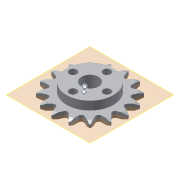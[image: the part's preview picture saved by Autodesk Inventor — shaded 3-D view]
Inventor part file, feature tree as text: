
AUTODESK INVENTOR PART (.ipt)
format: ipt  version: 2013 (Build 170138000, 138)  size: 427,520 bytes
history: native  units: in
note: dims shown in document units (in); Inventor stores cm internally (conversion verified against a paired STEP export)
features: other x17, plane x1
ambient origin geometry x8: Origin, YZ Plane, XZ Plane, XY Plane, X Axis, Y Axis, Z Axis, Center Point
bodies: Solid1 (feature_tree)
feature tree (18):
  other  "Tetrix sprocket 16T.ipt"
  other  "sprocket_25_16t_tetrix::Tetrix sprocket 16T.ipt"
  other  "TaggingFeature1"
  other  "FRONT"
  other  "TOP"
  other  "RIGHT"
  plane  "Work Plane4"
  other  "A_1"
  other  "A_2"
  other  "A_4"
  other  "A_5"
  other  "A_6"
  other  "A_3"
  other  "A_7"
  other  "A_8"
  other  "A_9"
  other  "iComposite:2"
  other  "iComposite:1"
